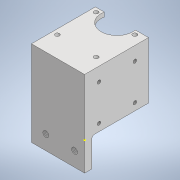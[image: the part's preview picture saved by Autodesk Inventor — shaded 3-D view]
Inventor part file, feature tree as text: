
AUTODESK INVENTOR PART (.ipt)
format: ipt  version: 2022 (Build 260153000, 153)  size: 229,376 bytes
history: native  units: mm
features: sketch x11, extrude x7, hole x3, fillet x3, other x1, projected_geometry x1
ambient origin geometry x8: Origin, YZ Plane, XZ Plane, XY Plane, X Axis, Y Axis, Z Axis, Center Point
bodies: Body1 (feature_tree)
feature tree (26):
  other  "ソリッド1"
  extrude  "押し出し1"  Depth=44.5mm
  extrude  "押し出し2"  Depth=34.0mm
  extrude  "押し出し3"  Depth=39.5mm TaperAngle=0.0deg
  extrude  "押し出し4"  Depth=3.0mm
  hole  "穴1"  [1 undecoded]
  fillet  "フィレット1"  Radius=33.5mm
  fillet  "フィレット2"  Radius=50.0mm
  sketch  "スケッチ7"
  extrude  "押し出し5"  Depth=43.5mm TaperAngle=0.0deg
  hole  "穴3"  [1 undecoded]
  extrude  "押し出し6"  Depth=2.0mm
  fillet  "フィレット4"  Radius=17.0mm
  extrude  "押し出し9"  Depth=3.0mm TaperAngle=0.0deg
  hole  "穴6"  [1 undecoded]
  sketch  "スケッチ1"
  sketch  "スケッチ2"
  sketch  "スケッチ3"
  sketch  "スケッチ4"
  sketch  "スケッチ5"
  sketch  "スケッチ8"
  sketch  "スケッチ9"
  sketch  "スケッチ11"
  projected_geometry  "投影ループ1"
  sketch  "スケッチ17"
  sketch  "スケッチ19"
note: 3 required parameter values undecoded (feature->parameter linkage not recoverable at this tier; creation-order binding heuristic only, values carry confidence <= 0.55)
